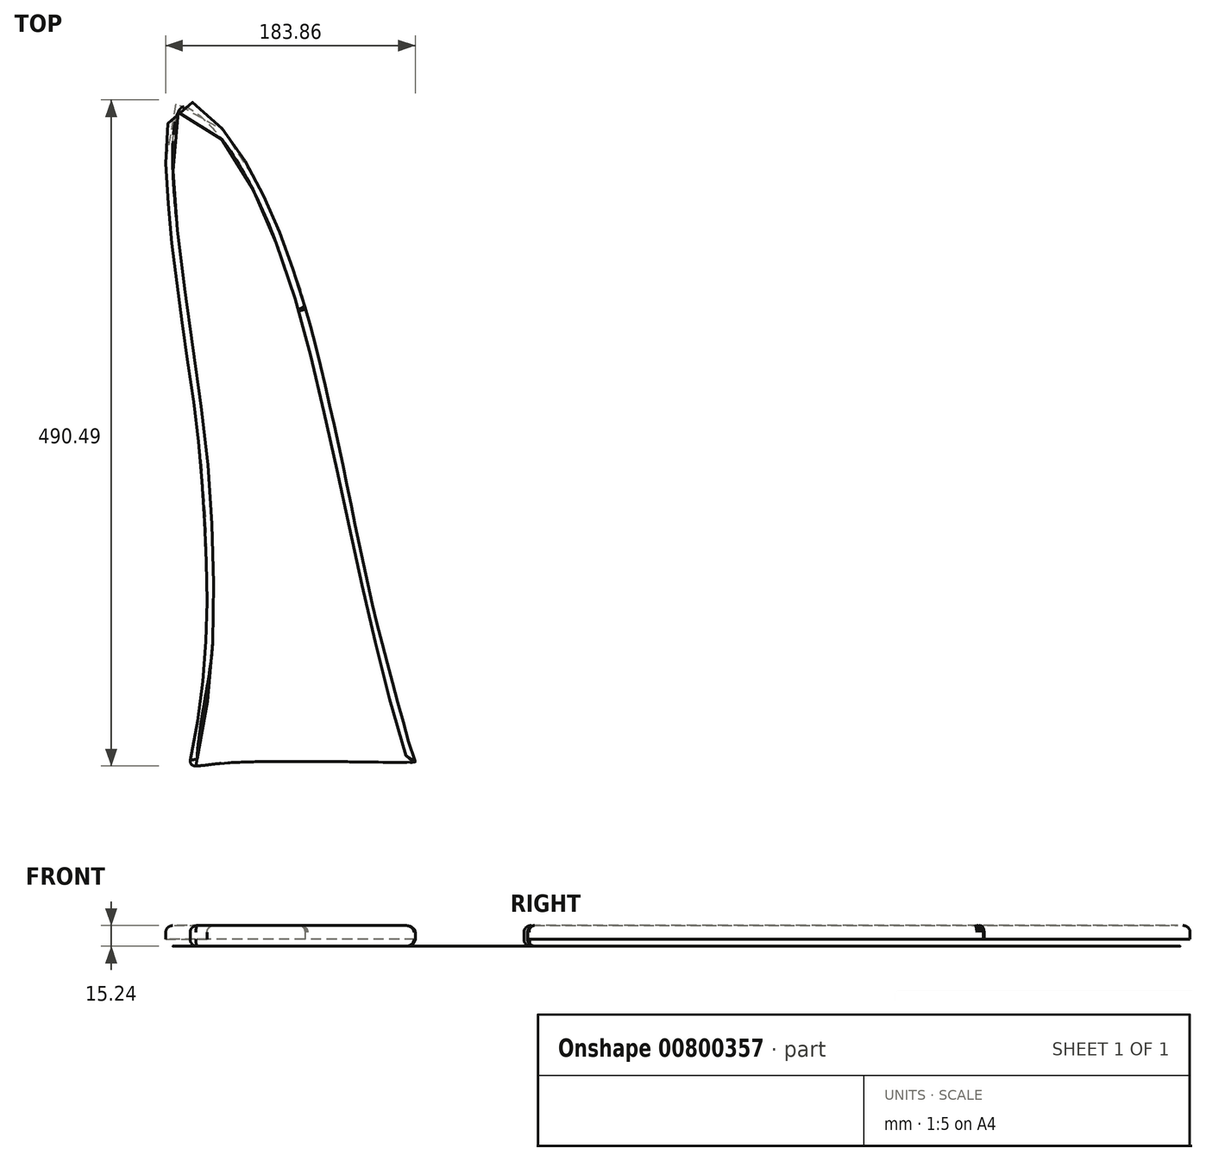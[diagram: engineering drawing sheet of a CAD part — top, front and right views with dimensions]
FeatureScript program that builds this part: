
annotation { "Feature Type Name" : "Feature", "Feature Type Description" : "" }
export const myFeature = defineFeature(function(context is Context, id is Id, definition is map)
    precondition{}
    {
        {
            var Q0;
            Q0=qCreatedBy(makeId("Top.planeOp"),FACE);
            var sketch = newSketch(context, id + "F0", { "sketchPlane" : qUnion([Q0])});
            skFitSpline(sketch, "E0", {"points": [v(80.63, -74.7) * mm, v(80.63, -74.03) * mm, v(49, 42.24) * mm, v(30.02, 132.7) * mm, v(0, 261.31) * mm, v(0, 260.6) * mm, v(-34.63, 350) * mm, v(-92.6, 412.26) * mm, v(-100.06, 324.6) * mm, v(-78.71, 163.55) * mm, v(-74.07, 105.53) * mm, v(-72.73, 60.26) * mm, v(-73.23, 13.32) * mm, v(-76.65, -19.2) * mm, v(-80.7, -51.78) * mm, v(-84.54, -75.7) * mm, v(-61.14, -75.7) * mm, v(80.63, -74.7) * mm]});
            skSolve(sketch);
        }
        {
            var Q0;
            Q0=makeQuery(id+"F0.imprint","IMPRINT",FACE,{"disambiguationData":[TD([[makeQuery(id+"F0.imprint","IMPRINT",EDGE,{"derivedFrom":sQuery(id+"F0.wireOp",EDGE,"E0")}),1.0]])]});
            extrude(context, id + "F1", {"entities" : qUnion([Q0]), "depth" : 15.24 * mm, "offsetDistance" : 25.4 * mm});
        }
        {
            var Q0;
            Q0=makeQuery(id+"F1.opExtrude","SWEPT_FACE",FACE,{"disambiguationData":[OSD([sQuery(id+"F0.wireOp",EDGE,"E0")])]});
            fillet(context, id + "F2", {"entities" : qUnion([Q0]), "radius" : 5.08 * mm, "tangentPropagation" : true, "allowEdgeOverflow" : false});
        }
    });
